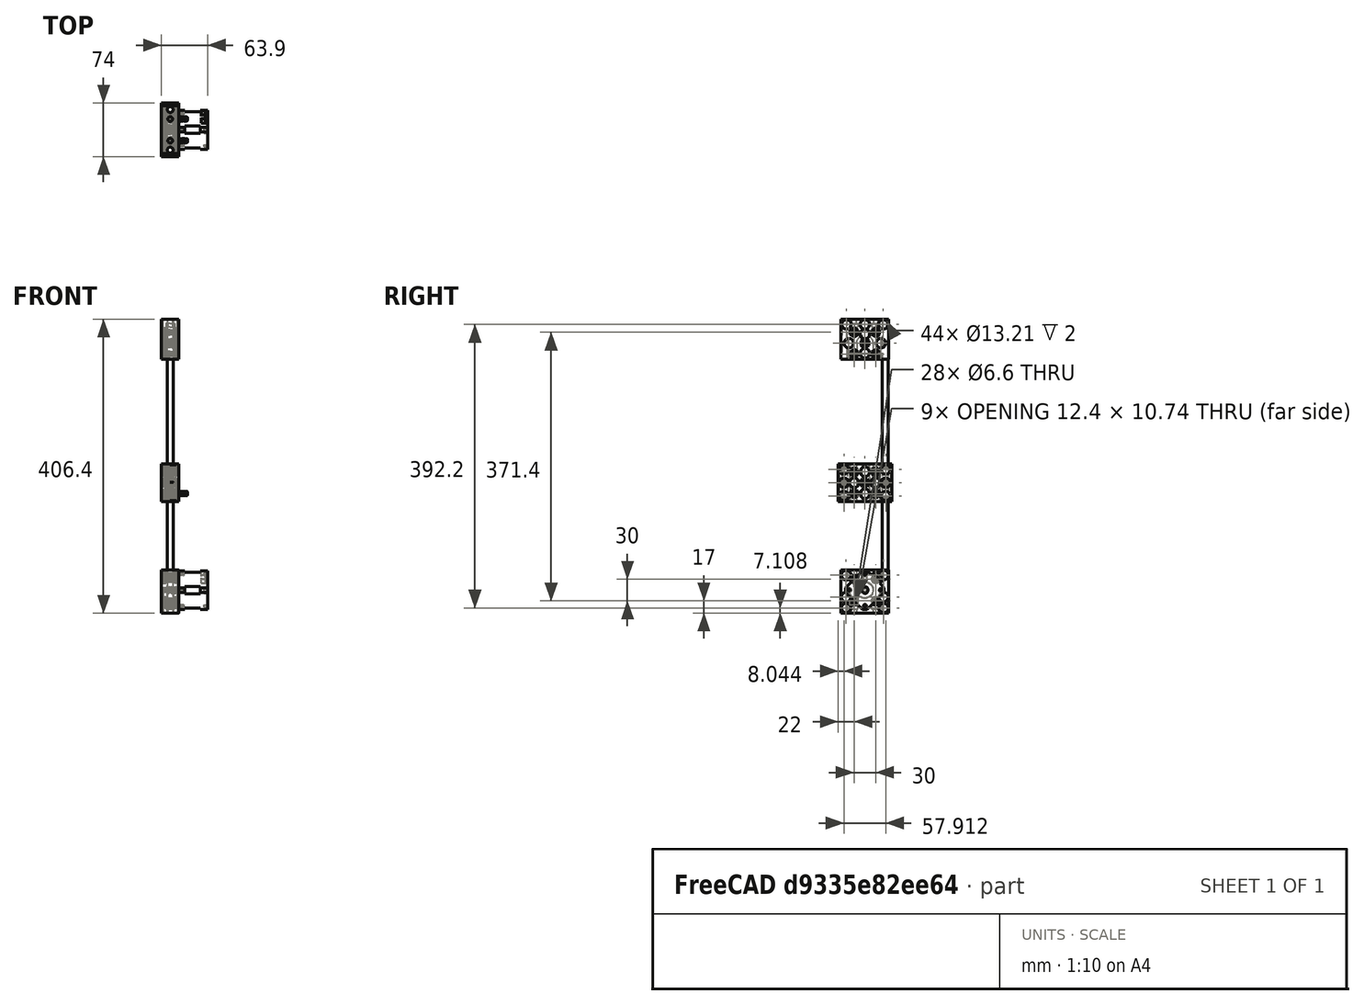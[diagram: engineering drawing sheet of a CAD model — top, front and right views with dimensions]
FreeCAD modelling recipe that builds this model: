
FCSTD DOCUMENT  (FreeCAD 0.16R6707 (Git))
Label: D3D  Z Axis
License: CreativeCommons Attribution
LicenseURL: http://creativecommons.org/licenses/by/4.0/
objects: Part::FeaturePython×29, Part::Feature×13, App::FeaturePython×4, Part::Mirroring×3, Part::MultiFuse×3, Part::Cylinder×1, App::DocumentObjectGroup×1
note: 49 computed .brp shape members not serialized (recipe doc carries the construction recipe); baked Part::Feature solids carry a one-line shape summary decoded from their .brp

FEATURE [Part::FeaturePython] Universal_axis_idler_side_01  # a2plus imported part (geometry in sourceFile) (typed FeaturePython)
  Placement = pos=(0,0,0) rot=(0.57735,0.57735,0.57735;2.0944rad)
  fixedPosition = true
  sourceFile = <userpath>/Downloads/Freecad/D3D Printer/Universal_axis_idler_side.fcstd
  timeLastImport = 1.48765e+09
  updateColors = true
FEATURE [Part::Mirroring] Part__Mirroring  label="Universal_axis_idler_side_01 (Mirror #1)"
  Base = (0,0,0)
  Normal = (1,0,0)
  Source = -> Universal_axis_idler_side_01
FEATURE [Part::MultiFuse] Fusion  label="Y1 Universal Axis Idler"
  Placement = pos=(12,33,-33) rot=(-1,0,0;1.5708rad)
  Shapes = -> [Part__Mirroring,Universal_axis_idler_side_01]
FEATURE [Part::Cylinder] Cylinder  label="Rod"
  Angle = 360
  Height = 406.4
  Placement = pos=(12,5,-1.61743e-05) rot=(0,1,0;3.14159rad)
  Radius = 3.96875
FEATURE [Part::FeaturePython] Clone006  label="Clone of Rod"  # Draft clone (typed FeaturePython)
  Objects = -> [Cylinder]
  Placement = pos=(11.9844,61,-1.61743e-05) rot=(1,0,0;3.14159rad)
  Scale = (1,1,1)
FEATURE [Part::FeaturePython] Universal_axis_motor_side_01  # a2plus imported part (geometry in sourceFile) (typed FeaturePython)
  fixedPosition = false
  sourceFile = <userpath>/Downloads/Freecad/D3D Printer/Universal_axis_motor_side.fcstd
  timeLastImport = 1.48765e+09
  updateColors = true
FEATURE [Part::Mirroring] Part__Mirroring003  label="Universal_axis_motor_side_01 (Mirror #3)"
  Base = (0,0,0)
  Normal = (0,0,1)
  Source = -> Universal_axis_motor_side_01
FEATURE [Part::MultiFuse] Fusion005  label="Y1 Universal Axis Motor"
  Placement = pos=(12,33,-374.4) rot=(0,-1,0;1.5708rad)
  Shapes = -> [Part__Mirroring003,Universal_axis_motor_side_01]
FEATURE [App::FeaturePython] planeConstraint01  label="Rods"  # a2plus constraint (typed FeaturePython)
  Object1 = Fusion005
  Object2 = Cylinder
  SubElement1 = Face3
  SubElement2 = Face2
  Type = plane
  directionConstraint = 0
  offset = 0
FEATURE [App::FeaturePython] planeConstraint02  label="Rods / Axis Motor "  # a2plus constraint (typed FeaturePython)
  Object1 = Fusion005
  Object2 = Clone006
  SubElement1 = Face42
  SubElement2 = Face2
  Type = plane
  directionConstraint = 0
  offset = 0
FEATURE [App::FeaturePython] planeConstraint03  label="Rods / Axis Idler"  # a2plus constraint (typed FeaturePython)
  Object1 = Fusion
  Object2 = Cylinder
  SubElement1 = Face3
  SubElement2 = Face3
  Type = plane
  directionConstraint = 1
  offset = 0
FEATURE [Part::FeaturePython] carriage_8mm_rods_01  # a2plus imported part (geometry in sourceFile) (typed FeaturePython)
  Placement = pos=(12.5,0,0) rot=(0,0,1;0rad)
  fixedPosition = false
  sourceFile = <userpath>/Downloads/Freecad/D3D Printer/Mess Stuff/axis_8mm STL + FCSTD/carriage_8mm_rods.FCStd
  timeLastImport = 1.48802e+09
  updateColors = true
FEATURE [Part::Mirroring] Part__Mirroring004  label="carriage_8mm_rods_01 (Mirror #3)"
  Base = (0,0,0)
  Normal = (0,0,1)
  Source = -> carriage_8mm_rods_01
FEATURE [Part::FeaturePython] M6_16_socket_bolt01  # a2plus imported part (geometry in sourceFile) (typed FeaturePython)
  Placement = pos=(3.66004e-06,18,-48) rot=(-0.57735,-0.57735,0.57735;2.0944rad)
  fixedPosition = false
  sourceFile = <userpath>/Downloads/Freecad/D3D Printer/Mess Stuff/M6-16 socket bolt.STEP
  timeLastImport = 1.48801e+09
  updateColors = true
FEATURE [Part::FeaturePython] M6_16_socket_bolt02  # a2plus imported part (geometry in sourceFile) (typed FeaturePython)
  Placement = pos=(3.66004e-06,18,-18) rot=(-0.57735,-0.57735,0.57735;2.0944rad)
  fixedPosition = false
  sourceFile = <userpath>/Downloads/Freecad/D3D Printer/Mess Stuff/M6-16 socket bolt.STEP
  timeLastImport = 1.48801e+09
  updateColors = true
FEATURE [Part::FeaturePython] M6_16_socket_bolt03  # a2plus imported part (geometry in sourceFile) (typed FeaturePython)
  Placement = pos=(8.1088e-06,33,-33) rot=(-0.57735,-0.57735,0.57735;2.0944rad)
  fixedPosition = false
  sourceFile = <userpath>/Downloads/Freecad/D3D Printer/Mess Stuff/M6-16 socket bolt.STEP
  timeLastImport = 1.48801e+09
  updateColors = true
FEATURE [Part::FeaturePython] M6_16_socket_bolt04  # a2plus imported part (geometry in sourceFile) (typed FeaturePython)
  Placement = pos=(1.25576e-05,48,-18) rot=(-0.57735,-0.57735,0.57735;2.0944rad)
  fixedPosition = false
  sourceFile = <userpath>/Downloads/Freecad/D3D Printer/Mess Stuff/M6-16 socket bolt.STEP
  timeLastImport = 1.48801e+09
  updateColors = true
FEATURE [Part::FeaturePython] M6_16_socket_bolt05  # a2plus imported part (geometry in sourceFile) (typed FeaturePython)
  Placement = pos=(1.25576e-05,48,-48) rot=(-0.57735,-0.57735,0.57735;2.0944rad)
  fixedPosition = false
  sourceFile = <userpath>/Downloads/Freecad/D3D Printer/Mess Stuff/M6-16 socket bolt.STEP
  timeLastImport = 1.48801e+09
  updateColors = true
FEATURE [Part::FeaturePython] M6_16_socket_bolt11  # a2plus imported part (geometry in sourceFile) (typed FeaturePython)
  Placement = pos=(1.25576e-05,48,-389.4) rot=(-0.57735,-0.57735,0.57735;2.0944rad)
  fixedPosition = false
  sourceFile = <userpath>/Downloads/Freecad/D3D Printer/Mess Stuff/M6-16 socket bolt.STEP
  timeLastImport = 1.48801e+09
  updateColors = true
FEATURE [Part::FeaturePython] M6_16_socket_bolt12  # a2plus imported part (geometry in sourceFile) (typed FeaturePython)
  Placement = pos=(1.25576e-05,48,-359.4) rot=(-0.57735,-0.57735,0.57735;2.0944rad)
  fixedPosition = false
  sourceFile = <userpath>/Downloads/Freecad/D3D Printer/Mess Stuff/M6-16 socket bolt.STEP
  timeLastImport = 1.48801e+09
  updateColors = true
FEATURE [Part::FeaturePython] M6_16_socket_bolt13  # a2plus imported part (geometry in sourceFile) (typed FeaturePython)
  Placement = pos=(3.66005e-06,18,-389.4) rot=(-0.57735,-0.57735,0.57735;2.0944rad)
  fixedPosition = false
  sourceFile = <userpath>/Downloads/Freecad/D3D Printer/Mess Stuff/M6-16 socket bolt.STEP
  timeLastImport = 1.48801e+09
  updateColors = true
FEATURE [Part::FeaturePython] M6_16_socket_bolt14  # a2plus imported part (geometry in sourceFile) (typed FeaturePython)
  Placement = pos=(3.66005e-06,18,-359.4) rot=(-0.57735,-0.57735,0.57735;2.0944rad)
  fixedPosition = false
  sourceFile = <userpath>/Downloads/Freecad/D3D Printer/Mess Stuff/M6-16 socket bolt.STEP
  timeLastImport = 1.48801e+09
  updateColors = true
FEATURE [Part::FeaturePython] m6_nut01  # a2plus imported part (geometry in sourceFile) (typed FeaturePython)
  Placement = pos=(3.5,18,-18) rot=(0.57735,-0.57735,0.57735;4.18879rad)
  fixedPosition = false
  sourceFile = <userpath>/Downloads/Freecad/D3D Printer/Mess Stuff/m6-nut.STEP
  timeLastImport = 1.48801e+09
  updateColors = true
FEATURE [Part::FeaturePython] m6_nut02  # a2plus imported part (geometry in sourceFile) (typed FeaturePython)
  Placement = pos=(3.5,18,-48) rot=(0.57735,-0.57735,0.57735;4.18879rad)
  fixedPosition = false
  sourceFile = <userpath>/Downloads/Freecad/D3D Printer/Mess Stuff/m6-nut.STEP
  timeLastImport = 1.48801e+09
  updateColors = true
FEATURE [Part::FeaturePython] m6_nut03  # a2plus imported part (geometry in sourceFile) (typed FeaturePython)
  Placement = pos=(3.50001,33,-33) rot=(0.57735,-0.57735,0.57735;4.18879rad)
  fixedPosition = false
  sourceFile = <userpath>/Downloads/Freecad/D3D Printer/Mess Stuff/m6-nut.STEP
  timeLastImport = 1.48801e+09
  updateColors = true
FEATURE [Part::FeaturePython] m6_nut04  # a2plus imported part (geometry in sourceFile) (typed FeaturePython)
  Placement = pos=(3.50001,48,-18) rot=(0.57735,-0.57735,0.57735;4.18879rad)
  fixedPosition = false
  sourceFile = <userpath>/Downloads/Freecad/D3D Printer/Mess Stuff/m6-nut.STEP
  timeLastImport = 1.48801e+09
  updateColors = true
FEATURE [Part::FeaturePython] m6_nut05  # a2plus imported part (geometry in sourceFile) (typed FeaturePython)
  Placement = pos=(3.50001,48,-48) rot=(0.57735,-0.57735,0.57735;4.18879rad)
  fixedPosition = false
  sourceFile = <userpath>/Downloads/Freecad/D3D Printer/Mess Stuff/m6-nut.STEP
  timeLastImport = 1.48801e+09
  updateColors = true
FEATURE [Part::FeaturePython] m6_nut11  # a2plus imported part (geometry in sourceFile) (typed FeaturePython)
  Placement = pos=(3,17.9688,-210.992) rot=(-0.447213,0.774597,-0.447214;1.82348rad)
  fixedPosition = false
  sourceFile = <userpath>/Downloads/Freecad/D3D Printer/Mess Stuff/m6-nut.STEP
  timeLastImport = 1.48801e+09
  updateColors = true
FEATURE [Part::Feature] Part__Feature001  label="Pulley"
  Placement = pos=(20,33,-374.4) rot=(0.357407,-0.357407,0.862856;1.71777rad)
  shape: bbox 11 x 12.62 x 12.62 mm, 94 faces (baked)
FEATURE [Part::Feature] Part__Feature002  label="MK8"
  Placement = pos=(16.9019,30.8284,-376.706) rot=(1,0,0;0.785398rad)
  shape: bbox 3 x 3.394 x 3.394 mm, 13 faces (baked)
FEATURE [Part::Feature] Part__Feature003  label="ball_bearing"
  Placement = pos=(14,33,-33) rot=(-0.57735,-0.57735,0.57735;2.0944rad)
  shape: bbox 8 x 13.6 x 13.6 mm, 82 faces (baked)
FEATURE [Part::FeaturePython] M6_16_socket_bolt08  # a2plus imported part (geometry in sourceFile) (typed FeaturePython)
  Placement = pos=(3.43117e-06,18,-211) rot=(-0.57735,-0.57735,0.57735;2.0944rad)
  fixedPosition = false
  sourceFile = <userpath>/Downloads/Freecad/D3D Printer/Mess Stuff/M6-16 socket bolt.STEP
  timeLastImport = 1.48801e+09
  updateColors = true
FEATURE [Part::Feature] Part__Feature004  label="lmuu 8mm bearing"
  Placement = pos=(0,-28,0) rot=(0,0,1;1.5708rad)
  shape: bbox 24 x 15 x 15 mm, 38 faces (baked)
FEATURE [Part::FeaturePython] Clone  label="lmuu 8mm bearing001"  # Draft clone (typed FeaturePython)
  Objects = -> [Part__Feature004]
  Placement = pos=(25,-28,0) rot=(0,0,1;1.5708rad)
  Scale = (1,1,1)
FEATURE [Part::FeaturePython] Clone007  label="lmuu 8mm bearing002"  # Draft clone (typed FeaturePython)
  Objects = -> [Part__Feature004]
  Placement = pos=(0,28,0) rot=(0,0,1;1.5708rad)
  Scale = (1,1,1)
FEATURE [Part::FeaturePython] Clone008  label="lmuu 8mm bearing003"  # Draft clone (typed FeaturePython)
  Objects = -> [Clone007]
  Placement = pos=(25,28,0) rot=(0,0,1;1.5708rad)
  Scale = (1,1,1)
FEATURE [Part::MultiFuse] Fusion006  label="Y1 Universal Axis Carriage"
  Placement = pos=(11.9844,33,-238.5) rot=(0,-1,0;1.5708rad)
  Shapes = -> [Part__Mirroring004,carriage_8mm_rods_01,Part__Feature004,Clone,Clone007,Clone008]
FEATURE [Part::FeaturePython] m6_nut06  # a2plus imported part (geometry in sourceFile) (typed FeaturePython)
  Placement = pos=(3.50001,48,-389.4) rot=(-0.447213,0.774597,-0.447214;1.82348rad)
  fixedPosition = false
  sourceFile = <userpath>/Downloads/Freecad/D3D Printer/Mess Stuff/m6-nut.STEP
  timeLastImport = 1.48801e+09
  updateColors = true
FEATURE [Part::FeaturePython] m6_nut07  # a2plus imported part (geometry in sourceFile) (typed FeaturePython)
  Placement = pos=(3.50001,48,-359.4) rot=(-0.447213,0.774597,-0.447214;1.82348rad)
  fixedPosition = false
  sourceFile = <userpath>/Downloads/Freecad/D3D Printer/Mess Stuff/m6-nut.STEP
  timeLastImport = 1.48801e+09
  updateColors = true
FEATURE [Part::FeaturePython] m6_nut08  # a2plus imported part (geometry in sourceFile) (typed FeaturePython)
  Placement = pos=(3.5,18,-359.4) rot=(-0.447213,0.774597,-0.447214;1.82348rad)
  fixedPosition = false
  sourceFile = <userpath>/Downloads/Freecad/D3D Printer/Mess Stuff/m6-nut.STEP
  timeLastImport = 1.48801e+09
  updateColors = true
FEATURE [Part::FeaturePython] m6_nut09  # a2plus imported part (geometry in sourceFile) (typed FeaturePython)
  Placement = pos=(3.5,18,-389.4) rot=(-0.447213,0.774597,-0.447214;1.82348rad)
  fixedPosition = false
  sourceFile = <userpath>/Downloads/Freecad/D3D Printer/Mess Stuff/m6-nut.STEP
  timeLastImport = 1.48801e+09
  updateColors = true
FEATURE [Part::Feature] m6_nut  label="m6_nut016"
  Placement = pos=(3.00001,32.9903,-226.018) rot=(-0.447213,0.774597,-0.447214;1.82348rad)
  shape: bbox 5.626 x 11.55 x 11.55 mm, 49 faces (baked)
FEATURE [Part::Feature] m6_nut015  label="m6_nut017"
  Placement = pos=(3.00001,47.9979,-210.986) rot=(-0.447213,0.774597,-0.447214;1.82348rad)
  shape: bbox 5.626 x 11.55 x 11.55 mm, 49 faces (baked)
FEATURE [App::DocumentObjectGroup] Group  label="nuts bolts"
  Group = -> [M6_16_socket_bolt01,M6_16_socket_bolt02,M6_16_socket_bolt03,M6_16_socket_bolt04,M6_16_socket_bolt05,M6_16_socket_bolt11,M6_16_socket_bolt12,M6_16_socket_bolt13,M6_16_socket_bolt14,m6_nut01,m6_nut02,m6_nut03,m6_nut04,m6_nut05,m6_nut11,M6_16_socket_bolt08,m6_nut06,m6_nut07,m6_nut08,m6_nut09,m6_nut,m6_nut015]
FEATURE [Part::FeaturePython] Clone009  label="Clone of M6_16_socket_bolt08"  # Draft clone (typed FeaturePython)
  Objects = -> [M6_16_socket_bolt08]
  Placement = pos=(1.23287e-05,48,-211) rot=(-0.57735,-0.57735,0.57735;2.0944rad)
  Scale = (1,1,1)
FEATURE [Part::FeaturePython] Clone010  label="Clone of M6_16_socket_bolt009"  # Draft clone (typed FeaturePython)
  Objects = -> [M6_16_socket_bolt08]
  Placement = pos=(7.87992e-06,33,-226) rot=(-0.57735,-0.57735,0.57735;2.0944rad)
  Scale = (1,1,1)
FEATURE [Part::Feature] Part__Feature006  label="M6x30"
  Placement = pos=(35.9844,47.9257,-241.06) rot=(0.57735,-0.57735,0.57735;4.18879rad)
  shape: bbox 36.21 x 10 x 10 mm, 148 faces (baked)
FEATURE [Part::Feature] Part__Feature007  label="M6x30 001"
  Placement = pos=(35.9844,18,-241) rot=(0.57735,-0.57735,0.57735;4.18879rad)
  shape: bbox 36.21 x 10 x 10 mm, 148 faces (baked)
FEATURE [Part::Feature] Part__Feature010  label="M3x25 screw002"
  Placement = pos=(31,32.9601,-352.483) rot=(0.57735,0.57735,-0.57735;4.18879rad)
  shape: bbox 27.72 x 6.495 x 6.495 mm, 290 faces (baked)
FEATURE [Part::Feature] Part__Feature011  label="M3x25 screw003"
  Placement = pos=(31,32.9751,-396.334) rot=(0.57735,0.57735,-0.57735;4.18879rad)
  shape: bbox 27.72 x 6.495 x 6.495 mm, 290 faces (baked)
FEATURE [Part::Feature] Part__Feature012  label="M3x25 screw004"
  Placement = pos=(31,54.9323,-374.374) rot=(0.57735,0.57735,-0.57735;4.18879rad)
  shape: bbox 27.72 x 6.495 x 6.495 mm, 290 faces (baked)
FEATURE [Part::Feature] Part__Feature  label="Nema 17 Step Motor"
  Placement = pos=(63.878,33,-374.4) rot=(0.678598,0.281085,-0.678598;3.68962rad)
  shape: bbox 61.88 x 53.46 x 53.46 mm, 81 faces (baked)
FEATURE [Part::Feature] Part__Feature013  label="M3x25 screw005"
  Placement = pos=(31,11.0781,-374.408) rot=(0.57735,0.57735,-0.57735;4.18879rad)
  shape: bbox 27.72 x 6.495 x 6.495 mm, 290 faces (baked)
FEATURE [App::FeaturePython] circularEdgeConstraint01  # a2plus constraint (typed FeaturePython)
  Object1 = Fusion005
  Object2 = Part__Feature
  SubElement1 = Edge21
  SubElement2 = Edge134
  Type = circularEdge
  directionConstraint = 0
  lockRotation = false
  offset = 0
